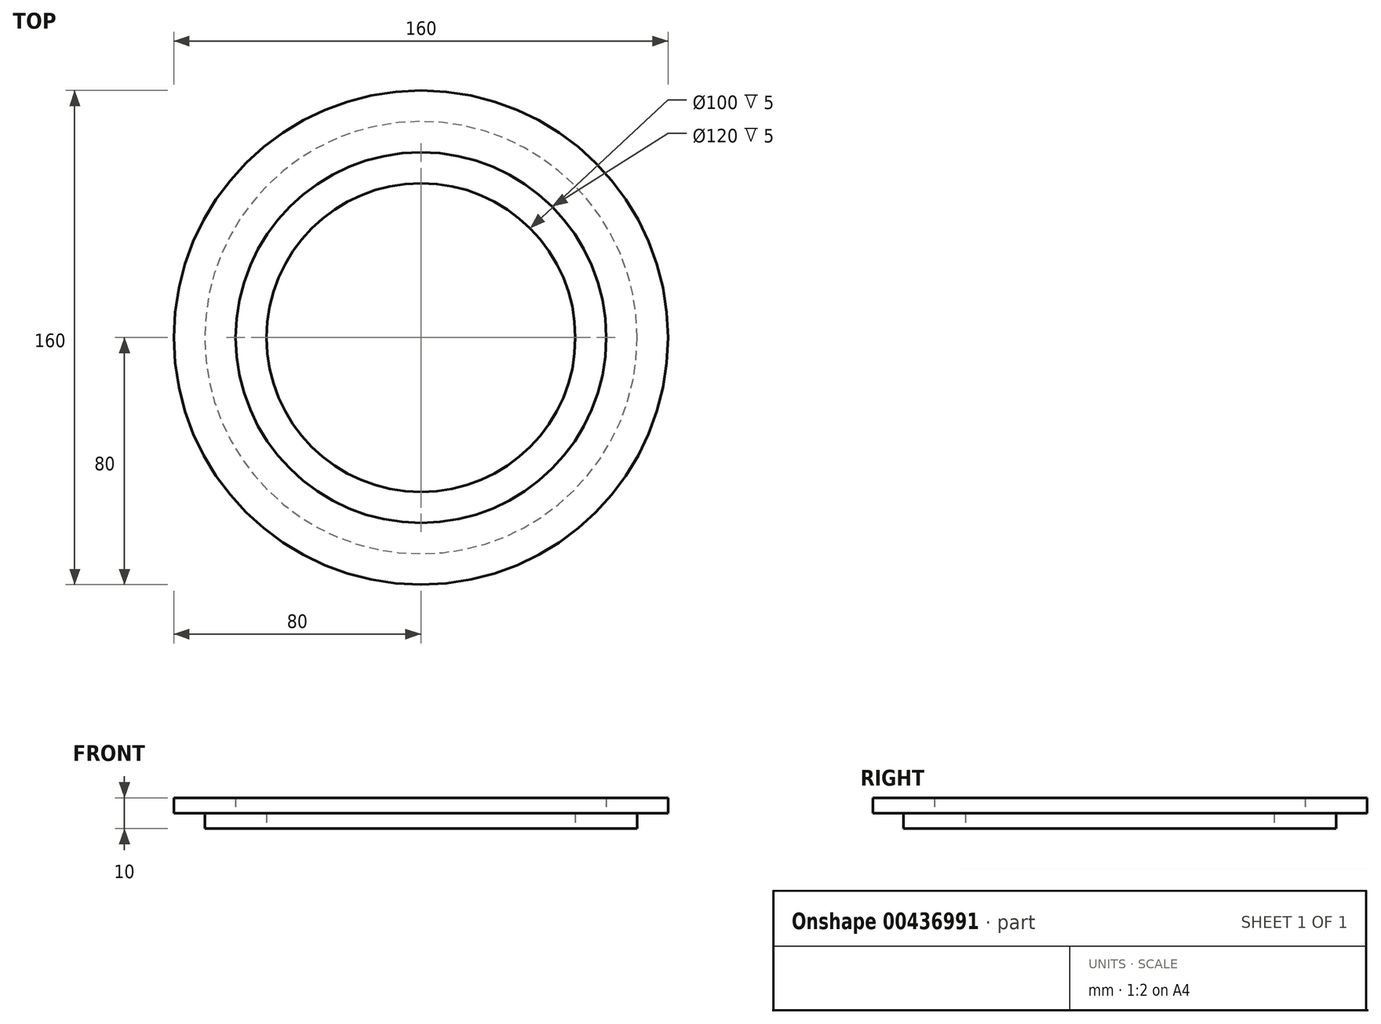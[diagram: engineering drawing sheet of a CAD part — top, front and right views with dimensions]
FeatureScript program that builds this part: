
annotation { "Feature Type Name" : "Feature", "Feature Type Description" : "" }
export const myFeature = defineFeature(function(context is Context, id is Id, definition is map)
    precondition{}
    {
        {
            var Q0;
            Q0=qCreatedBy(makeId("Front.planeOp"),FACE);
            var sketch = newSketch(context, id + "F0", { "sketchPlane" : qUnion([Q0])});
            skLineSegment(sketch, "E0", {"start": v(50, 0) * mm, "end": v(70, 0) * mm});
            skLineSegment(sketch, "E1", {"start": v(70, 0) * mm, "end": v(70, 5) * mm});
            skLineSegment(sketch, "E2", {"start": v(70, 5) * mm, "end": v(80, 5) * mm});
            skLineSegment(sketch, "E3", {"start": v(80, 5) * mm, "end": v(80, 10) * mm});
            skLineSegment(sketch, "E4", {"start": v(80, 10) * mm, "end": v(60, 10) * mm});
            skLineSegment(sketch, "E5", {"start": v(60, 10) * mm, "end": v(60, 5) * mm});
            skLineSegment(sketch, "E6", {"start": v(60, 5) * mm, "end": v(50, 5) * mm});
            skLineSegment(sketch, "E7", {"start": v(50, 5) * mm, "end": v(50, 0) * mm});
            skLineSegment(sketch, "E8", {"start": v(0, 0) * mm, "end": v(0, 62.26) * mm, "construction": true});
            skSolve(sketch);
        }
        {
            var Q0;
            Q0=makeQuery(id+"F0.imprint","IMPRINT",FACE,{"disambiguationData":[TD([[makeQuery(id+"F0.imprint","IMPRINT",EDGE,{"derivedFrom":sQuery(id+"F0.wireOp",EDGE,"E0")}),1.0]])]});
            var Q1;
            Q1=sQuery(id+"F0.wireOp",EDGE,"E8");
            revolve(context, id + "F1", {"entities" : qUnion([Q0]), "axis" : qUnion([Q1]), "revolveType" : RevolveType.FULL});
        }
    });
